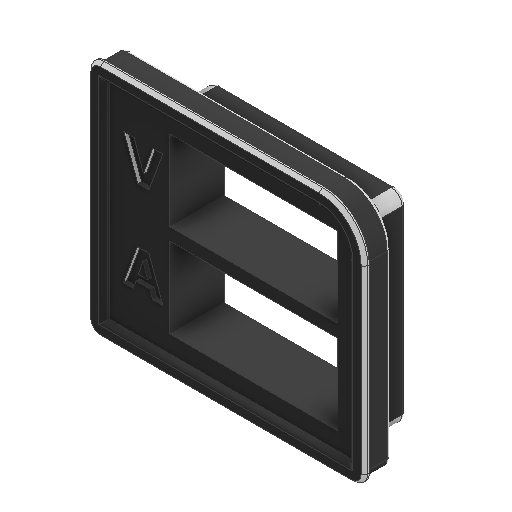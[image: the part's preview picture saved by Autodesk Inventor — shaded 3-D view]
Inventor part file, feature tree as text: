
AUTODESK INVENTOR PART (.ipt)
format: ipt  version: 2025 (Build 290162000, 162)  size: 364,032 bytes
history: native  units: mm
features: reference x51, sketch x9, extrude x6, other x6, fillet x2, emboss x1, sweep x1, projected_geometry x1
ambient origin geometry x8: Origin, YZ Plane, XZ Plane, XY Plane, X Axis, Y Axis, Z Axis, Center Point
bodies: Solid1 (feature_tree)
feature tree (77):
  extrude  "Extrusion1"  Depth=50.0mm
  extrude  "Extrusion2"  Depth=7.0mm TaperAngle=0.0deg
  extrude  "Extrusion3"  Depth=1.1mm
  extrude  "Extrusion4"  Depth=0.35mm
  extrude  "Extrusion5"  Depth=4.0mm TaperAngle=0.0deg
  extrude  "Extrusion6"  Depth=15.0mm
  emboss  "Emboss1"
  fillet  "Fillet3"  Radius=8.726646mm
  fillet  "Fillet2"  Radius=6.981317mm
  sweep  "Sweep3"
  sketch  "Sketch1"  dims[d0=60.0mm d1=50.0mm]
  sketch  "Sketch2"  dims[d2=7.0mm d3=0.0mm d6=7.0mm d7=0.0mm]
  sketch  "Sketch3"  dims[d8=1.1mm d9=0.0mm d10=3.0mm]
  reference  "Reference2"
  sketch  "Sketch4"  dims[d11=4.0mm d12=0.0mm d13=0.35mm]
  reference  "Reference3"
  reference  "Reference4"
  reference  "Reference5"
  reference  "Reference6"
  reference  "Reference7"
  reference  "Reference8"
  reference  "Reference9"
  reference  "Reference10"
  sketch  "Sketch5"  dims[d14=0.35mm d15=4.0mm d16=0.0mm]
  reference  "Reference11"
  reference  "Reference12"
  reference  "Reference13"
  reference  "Reference14"
  reference  "Reference15"
  reference  "Reference16"
  reference  "Reference17"
  reference  "Reference18"
  reference  "Reference21"
  reference  "Reference22"
  reference  "Reference23"
  reference  "Reference24"
  reference  "Reference25"
  reference  "Reference26"
  reference  "Reference27"
  reference  "Reference28"
  reference  "Reference29"
  reference  "Reference30"
  reference  "Reference31"
  reference  "Reference32"
  reference  "Reference33"
  reference  "Reference34"
  reference  "Reference35"
  reference  "Reference36"
  sketch  "Sketch11"  dims[d27=0.25mm d29=15.0mm d38=8.726646mm d39=6.981317mm]
  reference  "Reference37"
  sketch  "Sketch12"  dims[d40=0.3mm d43=0.75mm]
  reference  "Reference39"
  sketch  "Sketch13"  dims[d46=3.5mm d48=0.7mm d49=0.0mm d52=8.0mm d53=16.0mm d54=8.0mm d55=8.0mm d56=1.5mm d57=0.0mm d58=2.0mm d59=0.0mm d60=0.0mm d62=7.39429mm d64=1.26mm d65=7.3mm d66=3.5mm d67=7.026096mm d68=1.26mm]
  reference  "Reference40"
  reference  "Reference41"
  projected_geometry  "Projected Loop3"
  reference  "Reference42"
  reference  "Reference43"
  reference  "Reference44"
  reference  "Reference45"
  reference  "Reference46"
  reference  "Reference47"
  reference  "Reference48"
  reference  "Reference49"
  reference  "Reference50"
  reference  "Reference51"
  reference  "Reference52"
  reference  "Reference53"
  reference  "Reference54"
  reference  "Reference55"
  sketch  "3D Sketch3"
  other  "USB_C_PD_PPS_sink_with_enclosure.iam"
  other  "top_enclosure:1"
  other  "USB_C_PD_PPS_sink:1"
  other  "3461AS_3461AS-1:2"
  other  "3461AS_3461AS-1:1"
  other  "G800LW304032EU-Footprint-1_CMP-002-00028-3:1"
